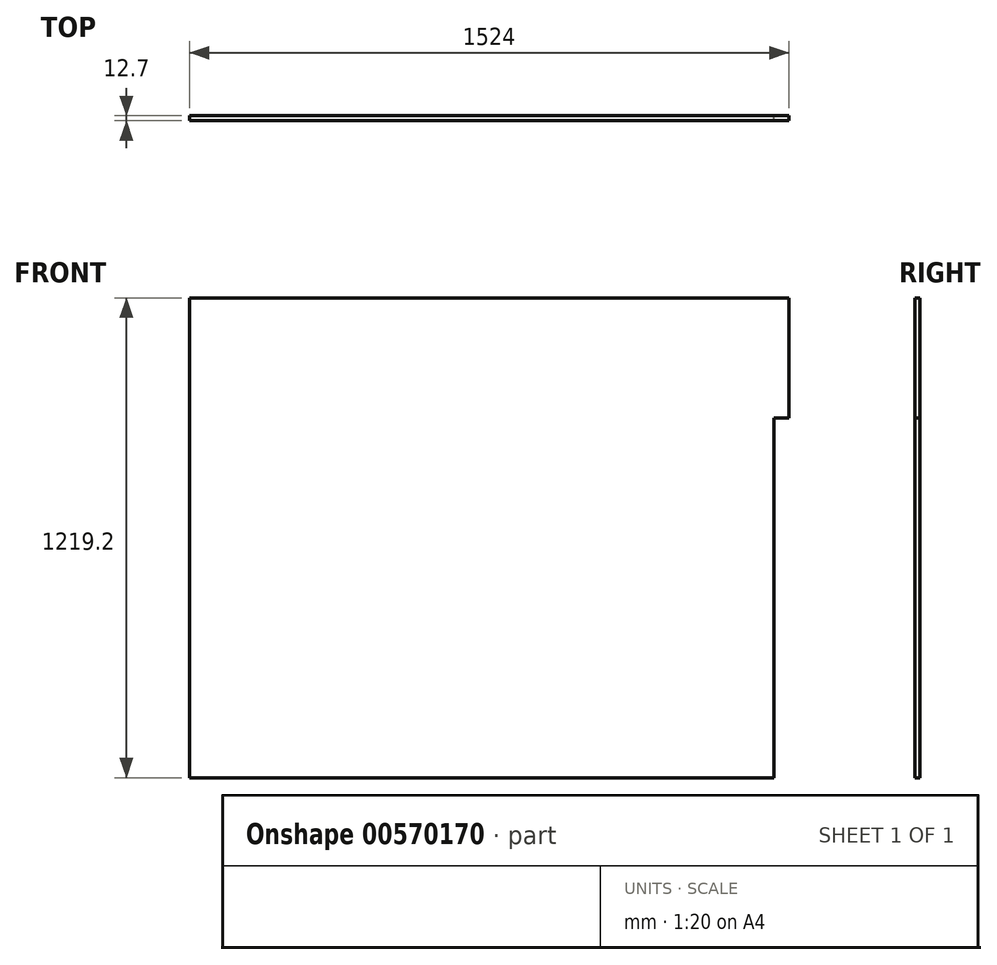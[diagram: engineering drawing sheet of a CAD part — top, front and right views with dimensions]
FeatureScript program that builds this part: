
annotation { "Feature Type Name" : "Feature", "Feature Type Description" : "" }
export const myFeature = defineFeature(function(context is Context, id is Id, definition is map)
    precondition{}
    {
        {
            var Q0;
            Q0=qCreatedBy(makeId("Front.planeOp"),FACE);
            var sketch = newSketch(context, id + "F0", { "sketchPlane" : qUnion([Q0])});
            skLineSegment(sketch, "E0.bottom", {"start": v(0, 0) * mm, "end": v(1485.9, 0) * mm});
            skLineSegment(sketch, "E0.top", {"start": v(0, 1219.2) * mm, "end": v(1524, 1219.2) * mm});
            skLineSegment(sketch, "E0.left", {"start": v(0, 0) * mm, "end": v(0, 1219.2) * mm});
            skLineSegment(sketch, "E1", {"start": v(1485.9, 0) * mm, "end": v(1485.9, 914.4) * mm});
            skLineSegment(sketch, "E2", {"start": v(1485.9, 914.4) * mm, "end": v(1524, 914.4) * mm});
            skLineSegment(sketch, "E3", {"start": v(1524, 914.4) * mm, "end": v(1524, 1219.2) * mm});
            skSolve(sketch);
        }
        {
            var Q0;
            Q0 = qSketchRegion(id + "F0", true);
            extrude(context, id + "F1", {"entities" : qUnion([Q0]), "depth" : 12.7 * mm, "offsetDistance" : 25.4 * mm});
        }
    });
